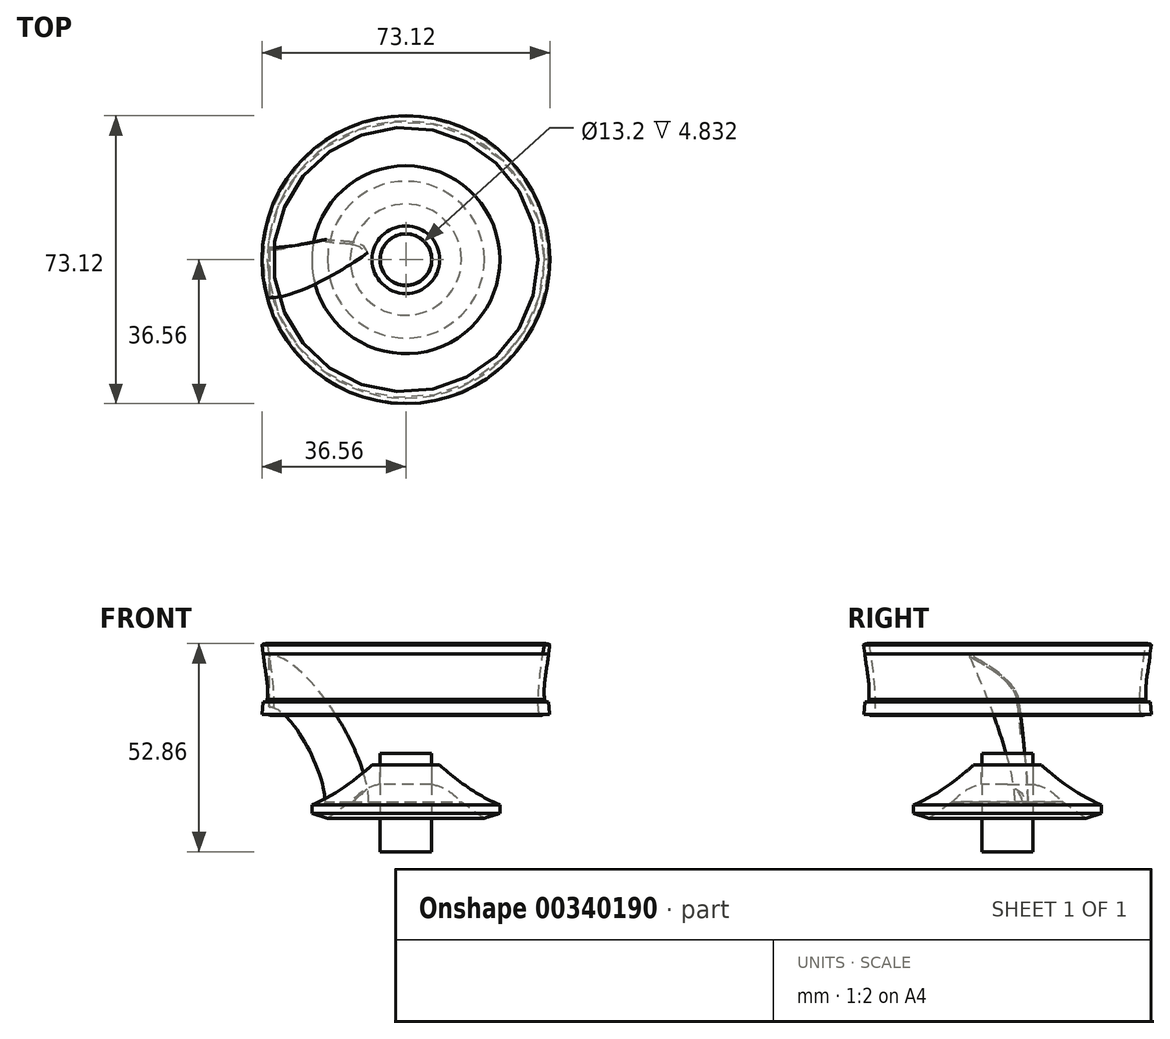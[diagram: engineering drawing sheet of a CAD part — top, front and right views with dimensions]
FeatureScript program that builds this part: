
annotation { "Feature Type Name" : "Feature", "Feature Type Description" : "" }
export const myFeature = defineFeature(function(context is Context, id is Id, definition is map)
    precondition{}
    {
        {
            var Q0;
            Q0=qCreatedBy(makeId("Front.planeOp"),FACE);
            var sketch = newSketch(context, id + "F0", { "sketchPlane" : qUnion([Q0])});
            skLineSegment(sketch, "E0", {"start": v(0, -4.1) * mm, "end": v(0, -8.94) * mm});
            skLineSegment(sketch, "E1", {"start": v(-6.6, -4.1) * mm, "end": v(-6.6, -8.94) * mm});
            skLineSegment(sketch, "E2", {"start": v(-23.88, -16.35) * mm, "end": v(-23.88, -14.16) * mm});
            skLineSegment(sketch, "E3", {"start": v(-6.6, -4.1) * mm, "end": v(-8.6, -4.1) * mm});
            skLineSegment(sketch, "E4", {"start": v(-23.88, -16.35) * mm, "end": v(-19.93, -17.58) * mm});
            skFitSpline(sketch, "E5", {"points": [v(-8.6, -4.1) * mm, v(-23.88, -14.16) * mm], "startDerivative": vector(-11.74, -10.23) * mm, "endDerivative": vector(-18.18, -7.06) * mm});
            skFitSpline(sketch, "E6", {"points": [v(-6.6, -8.94) * mm, v(-19.93, -17.58) * mm], "startDerivative": vector(-11.98, -4.68) * mm, "endDerivative": vector(-13.33, -8.64) * mm});
            skSolve(sketch);
        }
        {
            var Q0;
            Q0 = qSketchRegion(id + "F0", true);
            var Q1;
            Q1=sQuery(id+"F0.wireOp",EDGE,"E0");
            revolve(context, id + "F1", {"entities" : qUnion([Q0]), "axis" : qUnion([Q1]), "revolveType" : RevolveType.FULL});
        }
        {
            var Q0;
            Q0=qCreatedBy(makeId("Top.planeOp"),FACE);
            cPlane(context, id + "F2", {"entities" : qUnion([Q0]), "cplaneType" : CPlaneType.OFFSET, "offset" : 13.6 * mm, "oppositeDirection" : true, "width" : 150 * mm, "height" : 150 * mm});
        }
        {
            var Q0;
            Q0=qCreatedBy(id+"F2.planeOp",FACE);
            var sketch = newSketch(context, id + "F3", { "sketchPlane" : qUnion([Q0])});
            skCircle(sketch, "E7.0", {"center": v(0, 0) * mm, "radius": 23.88 * mm});
            skCircle(sketch, "E8.0", {"center": v(0, 0) * mm, "radius": 8.6 * mm});
            skFitSpline(sketch, "E9", {"points": [v(-10, 1.94) * mm, v(-20.3, 4.58) * mm], "startDerivative": vector(-4.16, 8.12) * mm, "endDerivative": vector(-10.3, 2.64) * mm});
            skFitSpline(sketch, "E10.0", {"points": [v(-9.47, 2.21) * mm, v(-9.68, 2.63) * mm, v(-10.27, 3.33) * mm, v(-11.46, 3.97) * mm, v(-12.82, 4.35) * mm, v(-14.31, 4.56) * mm, v(-15.86, 4.68) * mm, v(-17.4, 4.77) * mm, v(-18.88, 4.9) * mm, v(-19.76, 5.06) * mm, v(-20.16, 5.16) * mm]});
            skArc(sketch, "E11", {"start": v(-20.16, 5.16) * mm, "mid": v(-20.52, 4.95) * mm, "end": v(-20.3, 4.58) * mm});
            skArc(sketch, "E12", {"start": v(-10, 1.94) * mm, "mid": v(-9.6, 1.81) * mm, "end": v(-9.47, 2.21) * mm});
            skSolve(sketch);
        }
        {
            var Q0;
            Q0=qCreatedBy(makeId("Right.planeOp"),FACE);
            var sketch = newSketch(context, id + "F4", { "sketchPlane" : qUnion([Q0])});
            skLineSegment(sketch, "E13", {"start": v(-35.2, 12.54) * mm, "end": v(-35.2, 8.88) * mm});
            skFitSpline(sketch, "E14", {"points": [v(-36.24, 24.17) * mm, v(-35.2, 12.54) * mm], "startDerivative": vector(1.05, -11.63) * mm, "endDerivative": vector(-0.98, -13.92) * mm});
            skFitSpline(sketch, "E15", {"points": [v(-35.2, 8.88) * mm, v(-33.95, 8.88) * mm, v(-35.2, 26.33) * mm, v(-35.44, 26.73) * mm, v(-35.78, 26.74) * mm, v(-36.74, 26.33) * mm], "startDerivative": vector(10, -5.44) * mm, "endDerivative": vector(-4.47, -5.54) * mm});
            skLineSegment(sketch, "E16.0", {"start": v(-8.6, -4.1) * mm, "end": v(8.6, -4.1) * mm});
            skLineSegment(sketch, "E17", {"start": v(-36.74, 24.17) * mm, "end": v(-36.74, 26.33) * mm});
            skLineSegment(sketch, "E18", {"start": v(-36.24, 24.17) * mm, "end": v(-36.56, 26.48) * mm});
            skLineSegment(sketch, "E19", {"start": v(-35.2, 8.88) * mm, "end": v(-36.5, 8.76) * mm});
            skLineSegment(sketch, "E20", {"start": v(-36.5, 8.76) * mm, "end": v(-36.25, 11.93) * mm});
            skLineSegment(sketch, "E21", {"start": v(-36.25, 11.93) * mm, "end": v(-35.2, 12.14) * mm});
            skSolve(sketch);
        }
        {
            var Q0;
            Q0 = qSketchRegion(id + "F4", true);
            var Q1;
            Q1=sQuery(id+"F0.wireOp",EDGE,"E0");
            revolve(context, id + "F5", {"entities" : qUnion([Q0]), "axis" : qUnion([Q1]), "revolveType" : RevolveType.FULL});
        }
        {
            var Q0;
            Q0=qCreatedBy(makeId("Right.planeOp"),FACE);
            cPlane(context, id + "F6", {"entities" : qUnion([Q0]), "cplaneType" : CPlaneType.OFFSET, "offset" : 34.6 * mm, "oppositeDirection" : true, "width" : 150 * mm, "height" : 150 * mm});
        }
        {
            var Q0;
            Q0=qCreatedBy(id+"F6.planeOp",FACE);
            var sketch = newSketch(context, id + "F7", { "sketchPlane" : qUnion([Q0])});
            skLineSegment(sketch, "E22.0", {"start": v(-36.56, 26.48) * mm, "end": v(36.56, 26.48) * mm});
            skLineSegment(sketch, "E23.0", {"start": v(-35.25, 8.88) * mm, "end": v(35.25, 8.88) * mm});
            skFitSpline(sketch, "E24", {"points": [v(3.04, 10.94) * mm, v(-9.32, 23.83) * mm], "startDerivative": vector(0.9, 15.46) * mm, "endDerivative": vector(-19.82, 11.2) * mm});
            skFitSpline(sketch, "E25.0", {"points": [v(2.54, 10.97) * mm, v(2.57, 11.57) * mm, v(2.46, 12.72) * mm, v(1.8, 14.38) * mm, v(0.68, 15.99) * mm, v(-1.34, 18.08) * mm, v(-4.7, 20.57) * mm, v(-7.92, 22.46) * mm, v(-9.56, 23.4) * mm]});
            skArc(sketch, "E26", {"start": v(-9.32, 23.83) * mm, "mid": v(-9.66, 23.73) * mm, "end": v(-9.56, 23.4) * mm});
            skArc(sketch, "E27", {"start": v(2.54, 10.97) * mm, "mid": v(2.77, 10.7) * mm, "end": v(3.04, 10.94) * mm});
            skSolve(sketch);
        }
        {
            var Q0;
            Q0=makeQuery(id+"F7.imprint","IMPRINT",FACE,{"disambiguationData":[TD([[makeQuery(id+"F7.imprint","IMPRINT",EDGE,{"derivedFrom":sQuery(id+"F7.wireOp",EDGE,"E24")}),1.0]])]});
            extrude(context, id + "F8", {"entities" : qUnion([Q0]), "oppositeDirection" : true, "depth" : .1 * mm});
        }
        {
            var Q0;
            Q0=makeQuery(id+"F3.imprint","IMPRINT",FACE,{"disambiguationData":[TD([[makeQuery(id+"F3.imprint","IMPRINT",EDGE,{"derivedFrom":sQuery(id+"F3.wireOp",EDGE,"E9")}),-1.0]])]});
            extrude(context, id + "F9", {"entities" : qUnion([Q0]), "oppositeDirection" : true, "depth" : .1 * mm});
        }
        {
            var Q0;
            Q0=makeQuery(id+"F8.opExtrude","CAP_FACE",FACE,{"disambiguationData":[OSD([sQuery(id+"F7.wireOp",EDGE,"E24"),sQuery(id+"F7.wireOp",EDGE,"E25.0"),sQuery(id+"F7.wireOp",EDGE,"E26"),sQuery(id+"F7.wireOp",EDGE,"E27")])],"isStart":true});
            var Q1;
            Q1=makeQuery(id+"F9.opExtrude","CAP_FACE",FACE,{"disambiguationData":[OSD([sQuery(id+"F3.wireOp",EDGE,"E9"),sQuery(id+"F3.wireOp",EDGE,"E10.0"),sQuery(id+"F3.wireOp",EDGE,"E11"),sQuery(id+"F3.wireOp",EDGE,"E12")])],"isStart":true});
            loft(context, id + "F10", {"startCondition" : LoftEndDerivativeType.NORMAL_TO_PROFILE, "startMagnitude" : 1, "endCondition" : LoftEndDerivativeType.NORMAL_TO_PROFILE, "endMagnitude" : 1, "sheetProfilesArray" : [{ "sheetProfileEntities" : qUnion([Q0]) }, { "sheetProfileEntities" : qUnion([Q1]) }]});
        }
        {
            var Q0;
            Q0=qCreatedBy(makeId("Front.planeOp"),FACE);
            var sketch = newSketch(context, id + "F11", { "sketchPlane" : qUnion([Q0])});
            skFitSpline(sketch, "E28.0", {"points": [v(-6.6, -8.94) * mm, v(-10.6, -10.5) * mm, v(-15.49, -14.7) * mm, v(-19.93, -17.58) * mm]});
            skLineSegment(sketch, "E29", {"start": v(-6.6, -8.94) * mm, "end": v(0, -8.94) * mm});
            skLineSegment(sketch, "E30", {"start": v(0, -8.94) * mm, "end": v(0, -27.53) * mm});
            skLineSegment(sketch, "E31", {"start": v(0, -27.53) * mm, "end": v(-19.93, -17.58) * mm});
            skSolve(sketch);
        }
        {
            var Q0;
            Q0 = qSketchRegion(id + "F11", true);
            var Q1;
            Q1=sQuery(id+"F11.wireOp",EDGE,"E30");
            revolve(context, id + "F12", {"operationType" : NewBodyOperationType.REMOVE, "entities" : qUnion([Q0]), "axis" : qUnion([Q1]), "revolveType" : RevolveType.FULL, "oppositeDirection" : true});
        }
        {
            var Q0;
            Q0=qCreatedBy(id+"F2.planeOp",FACE);
            var sketch = newSketch(context, id + "F13", { "sketchPlane" : qUnion([Q0])});
            skCircle(sketch, "E32", {"center": v(0, 0) * mm, "radius": 6.5 * mm});
            skSolve(sketch);
        }
        {
            var Q0;
            Q0 = qSketchRegion(id + "F13", true);
            extrude(context, id + "F14", {"entities" : qUnion([Q0]), "endBound" : BoundingType.SYMMETRIC, "depth" : 25 * mm});
        }
    });
